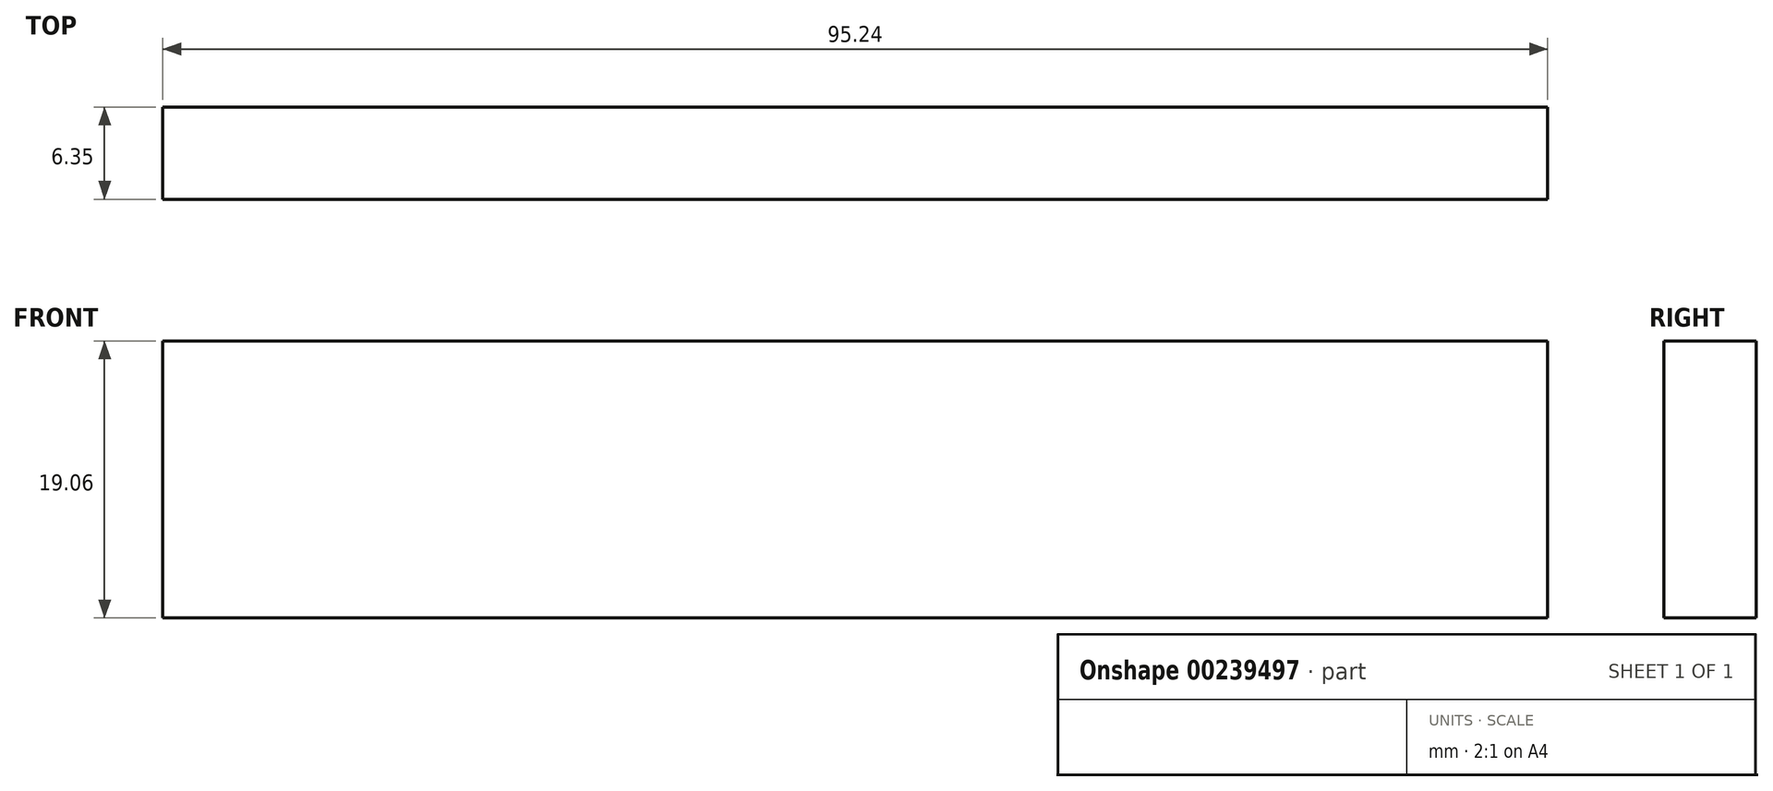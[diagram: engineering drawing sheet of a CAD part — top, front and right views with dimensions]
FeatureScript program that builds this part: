
annotation { "Feature Type Name" : "Feature", "Feature Type Description" : "" }
export const myFeature = defineFeature(function(context is Context, id is Id, definition is map)
    precondition{}
    {
        {
            var Q0;
            Q0=qCreatedBy(makeId("Front.planeOp"),FACE);
            var sketch = newSketch(context, id + "F0", { "sketchPlane" : qUnion([Q0])});
            skLineSegment(sketch, "E0.bottom", {"start": v(47.63, 9.52) * mm, "end": v(-47.63, 9.52) * mm});
            skLineSegment(sketch, "E0.top", {"start": v(47.63, -9.53) * mm, "end": v(-47.63, -9.53) * mm});
            skLineSegment(sketch, "E0.left", {"start": v(47.63, 9.52) * mm, "end": v(47.63, -9.53) * mm});
            skLineSegment(sketch, "E0.right", {"start": v(-47.63, 9.52) * mm, "end": v(-47.63, -9.53) * mm});
            skPoint(sketch, "E0.middle", {"position": v(0, 0) * mm});
            skSolve(sketch);
        }
        {
            var Q0;
            Q0 = qSketchRegion(id + "F0", true);
            extrude(context, id + "F1", {"entities" : qUnion([Q0]), "depth" : 6.35 * mm});
        }
    });
